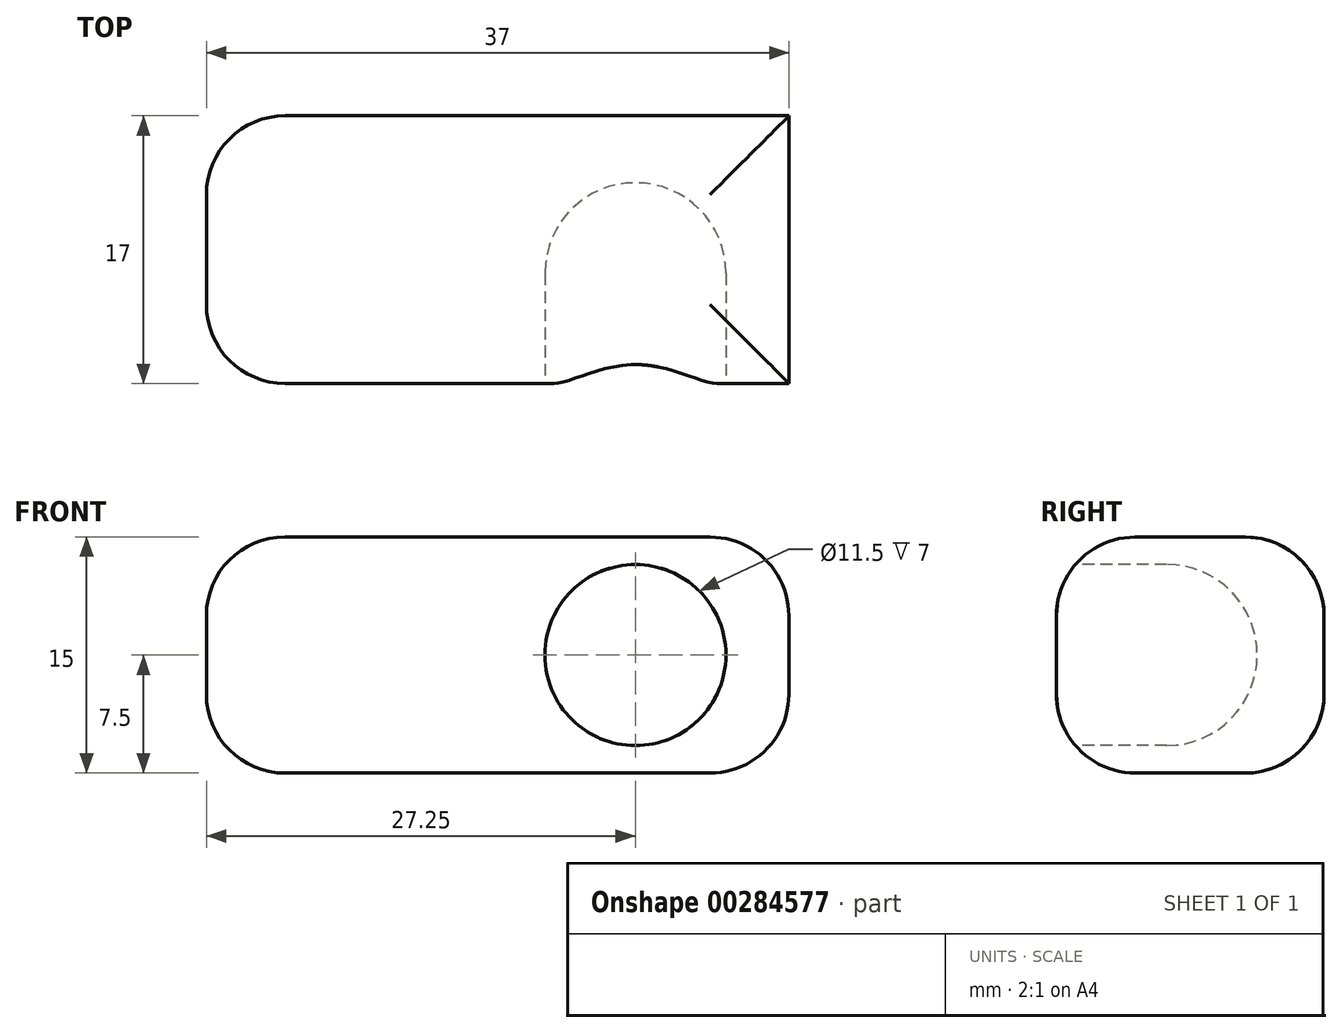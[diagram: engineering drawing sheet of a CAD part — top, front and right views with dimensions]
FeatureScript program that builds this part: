
annotation { "Feature Type Name" : "Feature", "Feature Type Description" : "" }
export const myFeature = defineFeature(function(context is Context, id is Id, definition is map)
    precondition{}
    {
        {
            var Q0;
            Q0=qCreatedBy(makeId("Front.planeOp"),FACE);
            var sketch = newSketch(context, id + "F0", { "sketchPlane" : qUnion([Q0])});
            skLineSegment(sketch, "E0.bottom", {"start": v(18.5, -7.5) * mm, "end": v(-18.5, -7.5) * mm});
            skLineSegment(sketch, "E0.top", {"start": v(18.5, 7.5) * mm, "end": v(-18.5, 7.5) * mm});
            skLineSegment(sketch, "E0.left", {"start": v(18.5, -7.5) * mm, "end": v(18.5, 7.5) * mm});
            skLineSegment(sketch, "E0.right", {"start": v(-18.5, -7.5) * mm, "end": v(-18.5, 7.5) * mm});
            skPoint(sketch, "E0.middle", {"position": v(0, 0) * mm});
            skSolve(sketch);
        }
        {
            var Q0;
            Q0=qSketchRegion(id+"F0",true);
            extrude(context, id + "F1", {"entities" : qUnion([Q0]), "depth" : 17 * mm});
        }
        {
            var Q0;
            Q0=makeQuery(id+"F1.opExtrude","CAP_FACE",FACE,{"disambiguationData":[OSD([sQuery(id+"F0.wireOp",EDGE,"E0.bottom"),sQuery(id+"F0.wireOp",EDGE,"E0.top"),sQuery(id+"F0.wireOp",EDGE,"E0.left"),sQuery(id+"F0.wireOp",EDGE,"E0.right")])],"isStart":false});
            var sketch = newSketch(context, id + "F2", { "sketchPlane" : qUnion([Q0])});
            skLineSegment(sketch, "E1", {"start": v(18.5, 0) * mm, "end": v(14.5, 0) * mm, "construction": true});
            skPoint(sketch, "E1.endSnap0", {"position": v(18.5, 0) * mm});
            skLineSegment(sketch, "E2", {"start": v(-18.5, 0) * mm, "end": v(3, 0) * mm, "construction": true});
            skLineSegment(sketch, "E3", {"start": v(3, 0) * mm, "end": v(14.5, 0) * mm, "construction": true});
            skCircle(sketch, "E4", {"center": v(8.75, 0) * mm, "radius": 5.75 * mm});
            skSolve(sketch);
        }
        {
            var Q0;
            Q0=makeQuery(id+"F2.imprint","IMPRINT",FACE,{"disambiguationData":[TD([[makeQuery(id+"F2.imprint","IMPRINT",EDGE,{"derivedFrom":sQuery(id+"F2.wireOp",EDGE,"E4")}),1.0]])]});
            extrude(context, id + "F3", {"entities" : qUnion([Q0]), "operationType" : NewBodyOperationType.REMOVE, "oppositeDirection" : true, "depth" : 7 * mm});
        }
        {
            var Q0;
            Q0=makeQuery(id+"F3.boolean.opBoolean","COPY",FACE,{"derivedFrom":makeQuery(id+"F3.opExtrude","CAP_FACE",FACE,{"disambiguationData":[OSD([sQuery(id+"F2.wireOp",EDGE,"E4")])],"isStart":false})});
            var sketch = newSketch(context, id + "F4", { "sketchPlane" : qUnion([Q0])});
            skCircle(sketch, "E5.0", {"center": v(8.75, 0) * mm, "radius": 5.75 * mm});
            skLineSegment(sketch, "E6", {"start": v(8.75, 0) * mm, "end": v(8.75, 5.75) * mm});
            skLineSegment(sketch, "E7", {"start": v(8.75, 0) * mm, "end": v(8.75, -5.75) * mm});
            skSolve(sketch);
        }
        {
            var Q0;
            {var subQ0=sQuery(id+"F4.wireOp",EDGE,"E6");Q0=makeQuery(id+"F4.imprint","IMPRINT",FACE,{"disambiguationData":[TD([[makeQuery(id+"F4.imprint","IMPRINT",EDGE,{"derivedFrom":subQ0}),1.0]])]});}
            var Q1;
            Q1=sQuery(id+"F4.wireOp",EDGE,"E6");
            revolve(context, id + "F5", {"operationType" : NewBodyOperationType.REMOVE, "entities" : qUnion([Q0]), "axis" : qUnion([Q1]), "revolveType" : RevolveType.FULL, "oppositeDirection" : true});
        }
        {
            var Q0;
            Q0=makeQuery(id+"F1.opExtrude","CAP_EDGE",EDGE,{"disambiguationData":[OSD([sQuery(id+"F0.wireOp",EDGE,"E0.top")])],"isStart":false});
            var Q1;
            Q1=makeQuery(id+"F1.opExtrude","CAP_EDGE",EDGE,{"disambiguationData":[OSD([sQuery(id+"F0.wireOp",EDGE,"E0.bottom")])],"isStart":false});
            var Q2;
            Q2=makeQuery(id+"F1.opExtrude","SWEPT_EDGE",EDGE,{"disambiguationData":[OSD([sQuery(id+"F0.wireOp",EDGE,"E0.top"),sQuery(id+"F0.wireOp",EDGE,"E0.left")])]});
            var Q3;
            Q3=makeQuery(id+"F1.opExtrude","SWEPT_EDGE",EDGE,{"disambiguationData":[OSD([sQuery(id+"F0.wireOp",EDGE,"E0.bottom"),sQuery(id+"F0.wireOp",EDGE,"E0.left")])]});
            var Q4;
            Q4=makeQuery(id+"F1.opExtrude","CAP_EDGE",EDGE,{"disambiguationData":[OSD([sQuery(id+"F0.wireOp",EDGE,"E0.top")])],"isStart":true});
            var Q5;
            Q5=makeQuery(id+"F1.opExtrude","CAP_EDGE",EDGE,{"disambiguationData":[OSD([sQuery(id+"F0.wireOp",EDGE,"E0.bottom")])],"isStart":true});
            var Q6;
            Q6=makeQuery(id+"F1.opExtrude","SWEPT_EDGE",EDGE,{"disambiguationData":[OSD([sQuery(id+"F0.wireOp",EDGE,"E0.top"),sQuery(id+"F0.wireOp",EDGE,"E0.right")])]});
            var Q7;
            Q7=makeQuery(id+"F1.opExtrude","CAP_EDGE",EDGE,{"disambiguationData":[OSD([sQuery(id+"F0.wireOp",EDGE,"E0.right")])],"isStart":false});
            var Q8;
            Q8=makeQuery(id+"F1.opExtrude","SWEPT_EDGE",EDGE,{"disambiguationData":[OSD([sQuery(id+"F0.wireOp",EDGE,"E0.bottom"),sQuery(id+"F0.wireOp",EDGE,"E0.right")])]});
            var Q9;
            Q9=makeQuery(id+"F1.opExtrude","CAP_EDGE",EDGE,{"disambiguationData":[OSD([sQuery(id+"F0.wireOp",EDGE,"E0.right")])],"isStart":true});
            fillet(context, id + "F6", {"entities" : qUnion([Q0, Q1, Q2, Q3, Q4, Q5, Q6, Q7, Q8, Q9]), "radius" : 5 * mm, "tangentPropagation" : true, "allowEdgeOverflow" : false});
        }
    });
